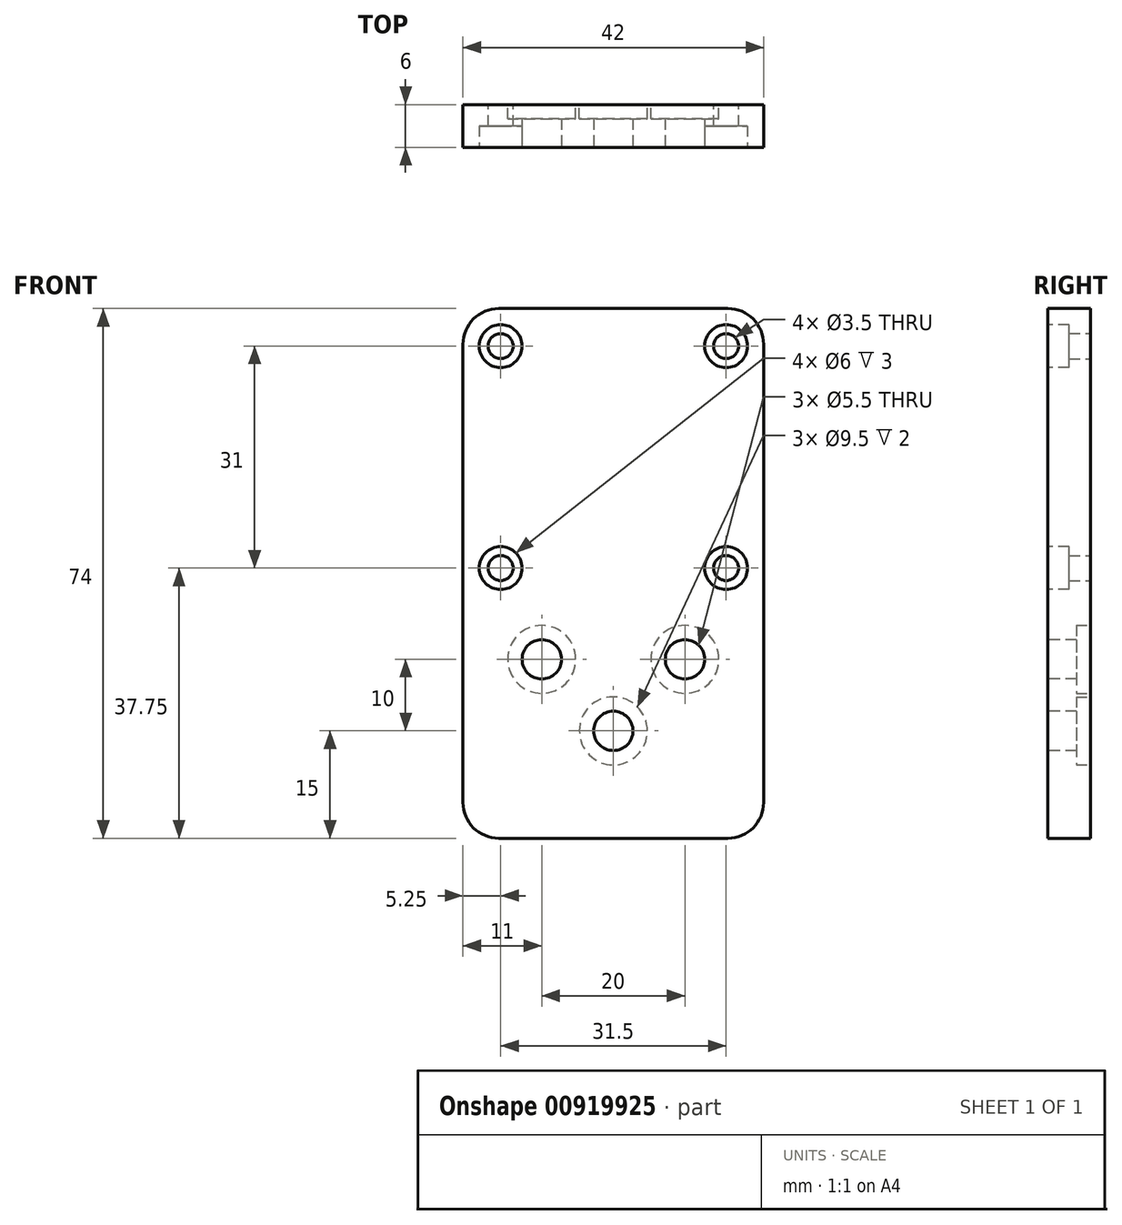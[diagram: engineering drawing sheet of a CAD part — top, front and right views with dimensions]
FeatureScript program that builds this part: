
annotation { "Feature Type Name" : "Feature", "Feature Type Description" : "" }
export const myFeature = defineFeature(function(context is Context, id is Id, definition is map)
    precondition{}
    {
        {
            var Q0;
            Q0=qCreatedBy(makeId("Front.planeOp"),FACE);
            var sketch = newSketch(context, id + "F0", { "sketchPlane" : qUnion([Q0])});
            skLineSegment(sketch, "E0.bottom", {"start": v(21, -37) * mm, "end": v(-21, -37) * mm});
            skLineSegment(sketch, "E0.top", {"start": v(21, 37) * mm, "end": v(-21, 37) * mm});
            skLineSegment(sketch, "E0.left", {"start": v(21, -37) * mm, "end": v(21, 37) * mm});
            skLineSegment(sketch, "E0.right", {"start": v(-21, -37) * mm, "end": v(-21, 37) * mm});
            skPoint(sketch, "E0.middle", {"position": v(0, 0) * mm});
            skLineSegment(sketch, "E1.left", {"start": v(-15.75, 0.25) * mm, "end": v(-15.75, -0.25) * mm, "construction": true});
            skLineSegment(sketch, "E1.right", {"start": v(15.75, 0.25) * mm, "end": v(15.75, -0.25) * mm, "construction": true});
            skCircle(sketch, "E2", {"center": v(-15.75, 31.75) * mm, "radius": 1.75 * mm});
            skCircle(sketch, "E3", {"center": v(15.75, 31.75) * mm, "radius": 1.75 * mm});
            skCircle(sketch, "E4", {"center": v(-15.75, 0.75) * mm, "radius": 1.75 * mm});
            skCircle(sketch, "E5", {"center": v(15.75, 0.75) * mm, "radius": 1.75 * mm});
            skSolve(sketch);
        }
        {
            var Q0;
            Q0=makeQuery(id+"F0.imprint","IMPRINT",FACE,{"disambiguationData":[TD([[makeQuery(id+"F0.imprint","IMPRINT",EDGE,{"derivedFrom":sQuery(id+"F0.wireOp",EDGE,"E0.bottom")}),-1.0]])]});
            extrude(context, id + "F1", {"entities" : qUnion([Q0]), "depth" : 6 * mm, "offsetDistance" : 25 * mm});
        }
        {
            var Q0;
            Q0=makeQuery(id+"F1.opExtrude","CAP_FACE",FACE,{"disambiguationData":[OSD([sQuery(id+"F0.wireOp",EDGE,"E0.bottom"),sQuery(id+"F0.wireOp",EDGE,"E0.top"),sQuery(id+"F0.wireOp",EDGE,"E0.left"),sQuery(id+"F0.wireOp",EDGE,"E0.right"),sQuery(id+"F0.wireOp",EDGE,"1xHXi7bt-C44v-ZIUs-zb9A-cx7KomL0weyG"),sQuery(id+"F0.wireOp",EDGE,"Ju0QJo4G-xHSc-B2tJ-YHhp-Y7aJ0lOTN4Ug"),sQuery(id+"F0.wireOp",EDGE,"1ji1FvfY-GHSN-739K-8OHd-5H8fEILQCvzC"),sQuery(id+"F0.wireOp",EDGE,"oFhJOTeH-80dY-KyvJ-5upA-F9iq5Y5RKmbn")])],"isStart":false});
            var sketch = newSketch(context, id + "F2", { "sketchPlane" : qUnion([Q0])});
            skCircle(sketch, "E6", {"center": v(-15.75, 31.75) * mm, "radius": 3 * mm});
            skCircle(sketch, "E7", {"center": v(15.75, 31.75) * mm, "radius": 3 * mm});
            skCircle(sketch, "E8", {"center": v(-15.75, 0.75) * mm, "radius": 3 * mm});
            skCircle(sketch, "E9", {"center": v(15.75, 0.75) * mm, "radius": 3 * mm});
            skLineSegment(sketch, "E10", {"start": v(43.17, -7) * mm, "end": v(-50.94, -7) * mm, "construction": true});
            skLineSegment(sketch, "E11", {"start": v(27.42, -12) * mm, "end": v(-29.36, -12) * mm, "construction": true});
            skLineSegment(sketch, "E12", {"start": v(0, -42.72) * mm, "end": v(0, 6.17) * mm, "construction": true});
            skPoint(sketch, "E12.startSnap0", {"position": v(0, -37) * mm});
            skSolve(sketch);
        }
        {
            var Q0;
            Q0=makeQuery(id+"F1.opExtrude","SWEPT_EDGE",EDGE,{"disambiguationData":[OSD([sQuery(id+"F0.wireOp",EDGE,"E0.bottom"),sQuery(id+"F0.wireOp",EDGE,"E0.right")])]});
            var Q1;
            Q1=makeQuery(id+"F1.opExtrude","SWEPT_EDGE",EDGE,{"disambiguationData":[OSD([sQuery(id+"F0.wireOp",EDGE,"E0.top"),sQuery(id+"F0.wireOp",EDGE,"E0.right")])]});
            var Q2;
            Q2=makeQuery(id+"F1.opExtrude","SWEPT_EDGE",EDGE,{"disambiguationData":[OSD([sQuery(id+"F0.wireOp",EDGE,"E0.top"),sQuery(id+"F0.wireOp",EDGE,"E0.left")])]});
            var Q3;
            Q3=makeQuery(id+"F1.opExtrude","SWEPT_EDGE",EDGE,{"disambiguationData":[OSD([sQuery(id+"F0.wireOp",EDGE,"E0.bottom"),sQuery(id+"F0.wireOp",EDGE,"E0.left")])]});
            fillet(context, id + "F3", {"entities" : qUnion([Q0, Q1, Q2, Q3]), "radius" : 5 * mm, "tangentPropagation" : true, "allowEdgeOverflow" : false});
        }
        {
            var Q0;
            Q0=makeQuery(id+"F2.imprint","IMPRINT",FACE,{"disambiguationData":[TD([[makeQuery(id+"F2.imprint","IMPRINT",EDGE,{"derivedFrom":sQuery(id+"F2.wireOp",EDGE,"E8")}),1.0]])]});
            var Q1;
            Q1=makeQuery(id+"F2.imprint","IMPRINT",FACE,{"disambiguationData":[TD([[makeQuery(id+"F2.imprint","IMPRINT",EDGE,{"derivedFrom":sQuery(id+"F2.wireOp",EDGE,"E9")}),1.0]])]});
            var Q2;
            Q2=makeQuery(id+"F2.imprint","IMPRINT",FACE,{"disambiguationData":[TD([[makeQuery(id+"F2.imprint","IMPRINT",EDGE,{"derivedFrom":sQuery(id+"F2.wireOp",EDGE,"E6")}),1.0]])]});
            var Q3;
            Q3=makeQuery(id+"F2.imprint","IMPRINT",FACE,{"disambiguationData":[TD([[makeQuery(id+"F2.imprint","IMPRINT",EDGE,{"derivedFrom":sQuery(id+"F2.wireOp",EDGE,"E7")}),1.0]])]});
            extrude(context, id + "F4", {"entities" : qUnion([Q0, Q1, Q2, Q3]), "operationType" : NewBodyOperationType.REMOVE, "oppositeDirection" : true, "depth" : 3 * mm, "offsetDistance" : 25 * mm});
        }
        {
            var Q0;
            Q0=makeQuery(id+"F1.opExtrude","CAP_FACE",FACE,{"disambiguationData":[OSD([sQuery(id+"F0.wireOp",EDGE,"E0.bottom"),sQuery(id+"F0.wireOp",EDGE,"E0.top"),sQuery(id+"F0.wireOp",EDGE,"E0.left"),sQuery(id+"F0.wireOp",EDGE,"E0.right"),sQuery(id+"F0.wireOp",EDGE,"E2"),sQuery(id+"F0.wireOp",EDGE,"E3"),sQuery(id+"F0.wireOp",EDGE,"E4"),sQuery(id+"F0.wireOp",EDGE,"E5")])],"isStart":false});
            var sketch = newSketch(context, id + "F5", { "sketchPlane" : qUnion([Q0])});
            skLineSegment(sketch, "E13", {"start": v(-27.08, 0) * mm, "end": v(35.72, 0) * mm, "construction": true});
            skLineSegment(sketch, "E14", {"start": v(0, 3.93) * mm, "end": v(0, -47.93) * mm, "construction": true});
            skCircle(sketch, "E15", {"center": v(0, -22) * mm, "radius": 2.75 * mm});
            skCircle(sketch, "E16", {"center": v(-10, -12) * mm, "radius": 2.75 * mm});
            skCircle(sketch, "E17", {"center": v(10, -12) * mm, "radius": 2.75 * mm});
            skLineSegment(sketch, "E18", {"start": v(-26.25, -12) * mm, "end": v(35.78, -12) * mm, "construction": true});
            skSolve(sketch);
        }
        {
            var Q0;
            Q0 = qSketchRegion(id + "F5", true);
            extrude(context, id + "F6", {"entities" : qUnion([Q0]), "operationType" : NewBodyOperationType.REMOVE, "endBound" : BoundingType.UP_TO_NEXT, "oppositeDirection" : true, "depth" : 25 * mm, "offsetDistance" : 25 * mm});
        }
        {
            var Q0;
            Q0=makeQuery(id+"F1.opExtrude","CAP_FACE",FACE,{"disambiguationData":[OSD([sQuery(id+"F0.wireOp",EDGE,"E0.bottom"),sQuery(id+"F0.wireOp",EDGE,"E0.top"),sQuery(id+"F0.wireOp",EDGE,"E0.left"),sQuery(id+"F0.wireOp",EDGE,"E0.right"),sQuery(id+"F0.wireOp",EDGE,"E2"),sQuery(id+"F0.wireOp",EDGE,"E3"),sQuery(id+"F0.wireOp",EDGE,"E4"),sQuery(id+"F0.wireOp",EDGE,"E5")])],"isStart":true});
            var sketch = newSketch(context, id + "F7", { "sketchPlane" : qUnion([Q0])});
            skCircle(sketch, "E19", {"center": v(-10, -12) * mm, "radius": 4.75 * mm});
            skCircle(sketch, "E20", {"center": v(10, -12) * mm, "radius": 4.75 * mm});
            skCircle(sketch, "E21", {"center": v(0, -22) * mm, "radius": 4.75 * mm});
            skSolve(sketch);
        }
        {
            var Q0;
            Q0 = qSketchRegion(id + "F7", true);
            extrude(context, id + "F8", {"entities" : qUnion([Q0]), "operationType" : NewBodyOperationType.REMOVE, "oppositeDirection" : true, "depth" : 2 * mm, "offsetDistance" : 25 * mm});
        }
    });
